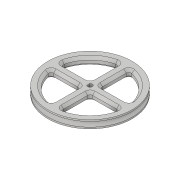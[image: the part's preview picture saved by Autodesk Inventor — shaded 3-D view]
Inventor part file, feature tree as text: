
AUTODESK INVENTOR PART (.ipt)
format: ipt  version: 2017 (Build 210142000, 142)  size: 233,984 bytes
history: native  units: in
note: dims shown in document units (in); Inventor stores cm internally (conversion verified against a paired STEP export)
features: sketch x3, extrude x2, revolve x1, fillet x1, chamfer x1
ambient origin geometry x8: Origin, YZ Plane, XZ Plane, XY Plane, X Axis, Y Axis, Z Axis, Center Point
bodies: Solid1 (feature_tree)
feature tree (8):
  revolve  "Revolution1"  [1 undecoded]
  extrude  "Extrusion1"  TaperAngle=90.0deg  [1 undecoded]
  extrude  "Extrusion2"  Depth=0.0624in
  fillet  "Fillet1"  Radius=1.0in
  chamfer  "Chamfer1"  Distance=0.115in
  sketch  "Sketch1"  dims[d0=0.2in d1=1.0625in]
  sketch  "Sketch2"  dims[d2=0.125in d3=90.0deg]
  sketch  "Sketch3"  dims[d4=1.75in d5=0.125in d6=0.125in d7=0.125in d8=0.125in d9=1.0in d10=0.0in d11=0.115in d12=0.0425in d13=1.0in d14=0.0in d15=0.0624in d16=0.0624in d17=0.125in d18=45.0deg]
note: 2 required parameter values undecoded (feature->parameter linkage not recoverable at this tier; creation-order binding heuristic only, values carry confidence <= 0.55)